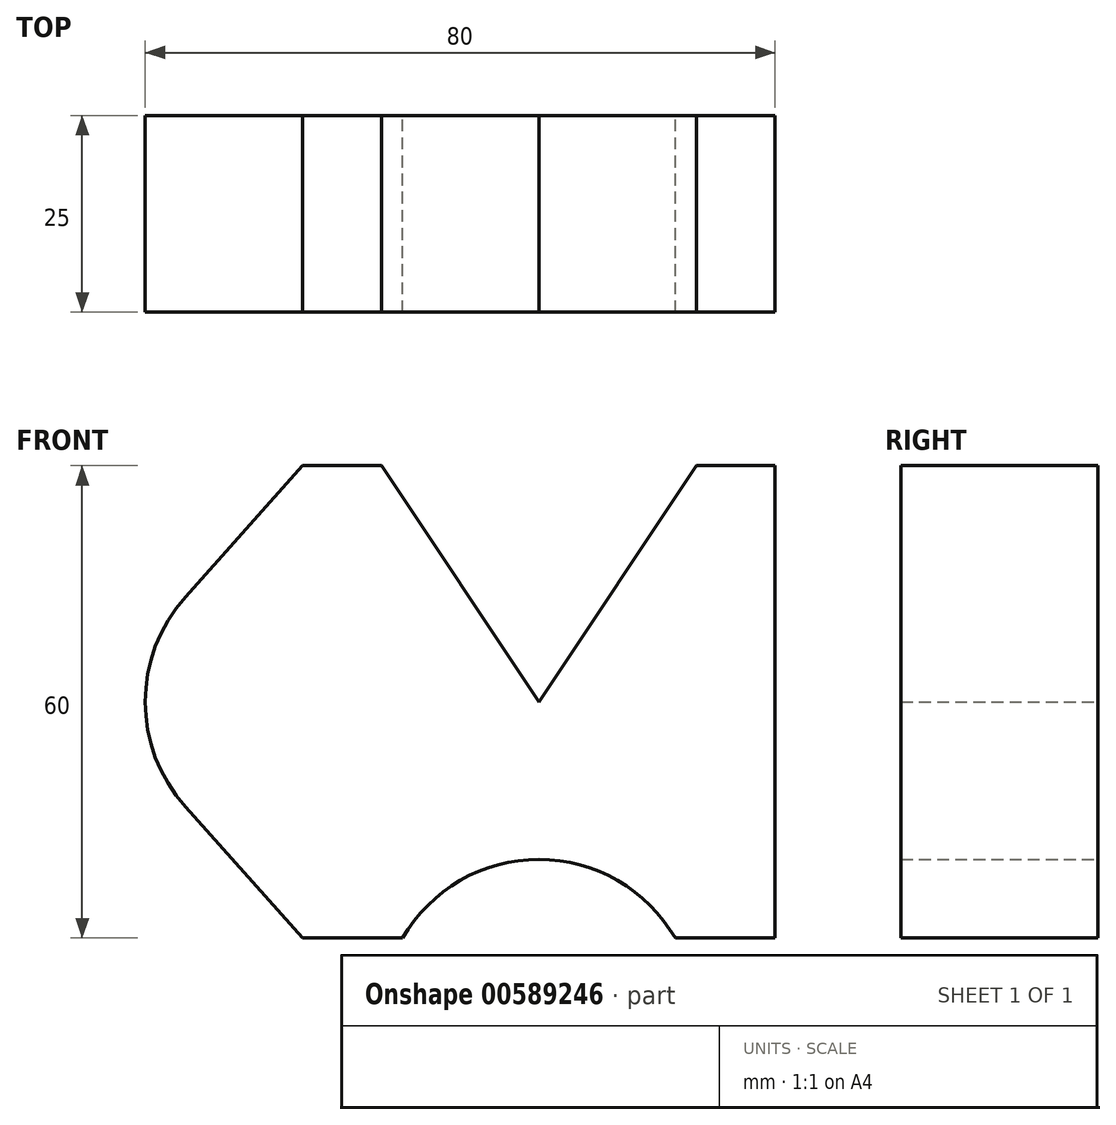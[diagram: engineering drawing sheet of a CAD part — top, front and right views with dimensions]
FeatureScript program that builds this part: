
annotation { "Feature Type Name" : "Feature", "Feature Type Description" : "" }
export const myFeature = defineFeature(function(context is Context, id is Id, definition is map)
    precondition{}
    {
        {
            var Q0;
            Q0=qCreatedBy(makeId("Front.planeOp"),FACE);
            var sketch = newSketch(context, id + "F0", { "sketchPlane" : qUnion([Q0])});
            skLineSegment(sketch, "E0", {"start": v(-44.9, 13.33) * mm, "end": v(-30, 30) * mm});
            skLineSegment(sketch, "E1", {"start": v(-30, 30) * mm, "end": v(-20, 30) * mm});
            skLineSegment(sketch, "E2", {"start": v(-20, 30) * mm, "end": v(0, 0) * mm});
            skLineSegment(sketch, "E3", {"start": v(0, 0) * mm, "end": v(20, 30) * mm});
            skLineSegment(sketch, "E4", {"start": v(20, 30) * mm, "end": v(30, 30) * mm});
            skLineSegment(sketch, "E5", {"start": v(30, 30) * mm, "end": v(30, -30) * mm});
            skLineSegment(sketch, "E6", {"start": v(30, -30) * mm, "end": v(17.32, -30) * mm});
            skLineSegment(sketch, "E7", {"start": v(-17.32, -30) * mm, "end": v(-30, -30) * mm});
            skLineSegment(sketch, "E8", {"start": v(-30, -30) * mm, "end": v(-44.9, -13.33) * mm});
            skArc(sketch, "E9", {"start": v(-44.9, 13.33) * mm, "mid": v(-50, 0) * mm, "end": v(-44.9, -13.33) * mm});
            skArc(sketch, "E10", {"start": v(17.32, -30) * mm, "mid": v(0, -20) * mm, "end": v(-17.32, -30) * mm});
            skLineSegment(sketch, "E11", {"start": v(-30, 37.43) * mm, "end": v(-30, -85.63) * mm, "construction": true});
            skSolve(sketch);
        }
        {
            var Q0;
            Q0 = qSketchRegion(id + "F0", true);
            extrude(context, id + "F1", {"entities" : qUnion([Q0]), "depth" : 25 * mm, "offsetDistance" : 25 * mm});
        }
    });
